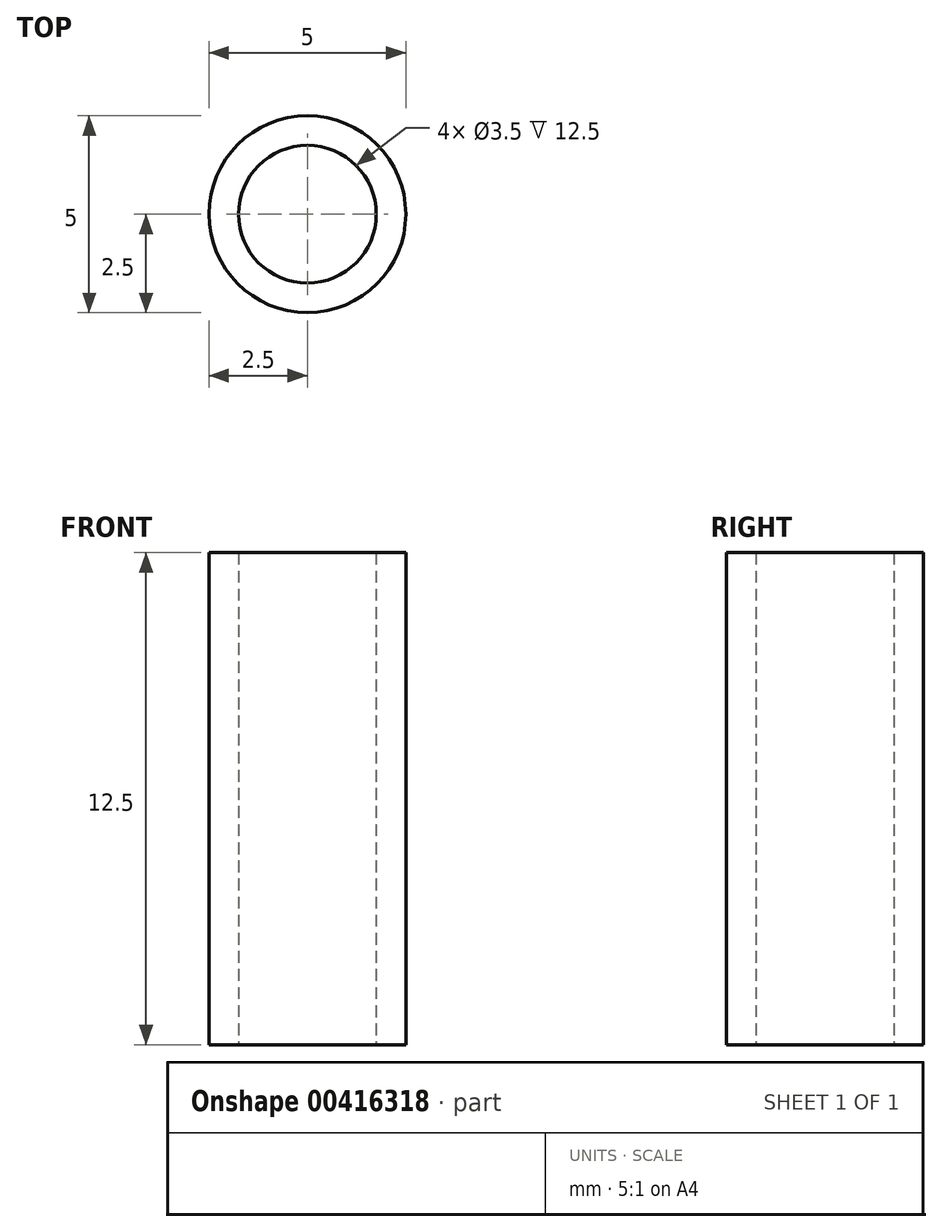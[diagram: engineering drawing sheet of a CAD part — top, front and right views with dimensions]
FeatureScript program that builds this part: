
annotation { "Feature Type Name" : "Feature", "Feature Type Description" : "" }
export const myFeature = defineFeature(function(context is Context, id is Id, definition is map)
    precondition{}
    {
        {
            var Q0;
            Q0=qCreatedBy(makeId("Top.planeOp"),FACE);
            var sketch = newSketch(context, id + "F0", { "sketchPlane" : qUnion([Q0])});
            skCircle(sketch, "E0", {"center": v(0, 0) * mm, "radius": 2.5 * mm});
            skCircle(sketch, "E1", {"center": v(0, 0) * mm, "radius": 1.75 * mm});
            skSolve(sketch);
        }
        {
            var Q0;
            Q0=makeQuery(id+"F0.imprint","IMPRINT",FACE,{"disambiguationData":[TD([[makeQuery(id+"F0.imprint","IMPRINT",EDGE,{"derivedFrom":sQuery(id+"F0.wireOp",EDGE,"E0")}),1.0]])]});
            extrude(context, id + "F1", {"entities" : qUnion([Q0]), "depth" : 12.5 * mm});
        }
    });
